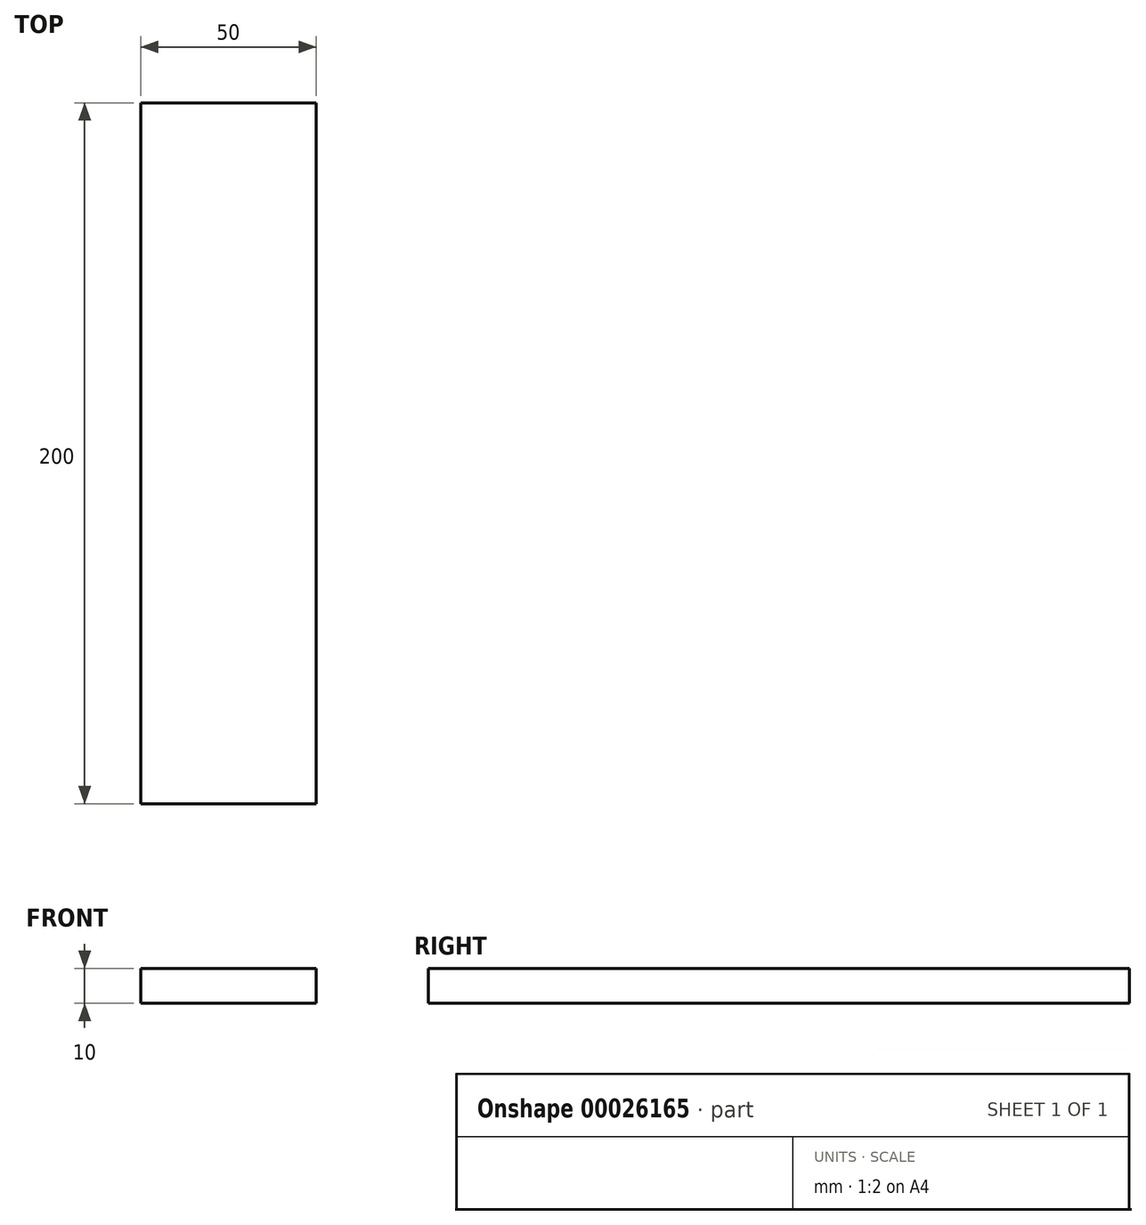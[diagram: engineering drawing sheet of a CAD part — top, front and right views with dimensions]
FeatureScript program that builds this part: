
annotation { "Feature Type Name" : "Feature", "Feature Type Description" : "" }
export const myFeature = defineFeature(function(context is Context, id is Id, definition is map)
    precondition{}
    {
        {
            var Q0;
            Q0=qCreatedBy(makeId("Top.planeOp"),FACE);
            var sketch = newSketch(context, id + "F0", { "sketchPlane" : qUnion([Q0])});
            skLineSegment(sketch, "E0.rect.bottom", {"start": v(25, 100) * mm, "end": v(-25, 100) * mm});
            skLineSegment(sketch, "E0.rect.top", {"start": v(25, -100) * mm, "end": v(-25, -100) * mm});
            skLineSegment(sketch, "E0.rect.left", {"start": v(25, 100) * mm, "end": v(25, -100) * mm});
            skLineSegment(sketch, "E0.rect.right", {"start": v(-25, 100) * mm, "end": v(-25, -100) * mm});
            skPoint(sketch, "E0.rect.middle", {"position": v(0, 0) * mm});
            skSolve(sketch);
        }
        {
            var Q0;
            Q0 = qSketchRegion(id + "F0", true);
            extrude(context, id + "F1", {"entities" : qUnion([Q0]), "depth" : 10 * mm});
        }
    });
